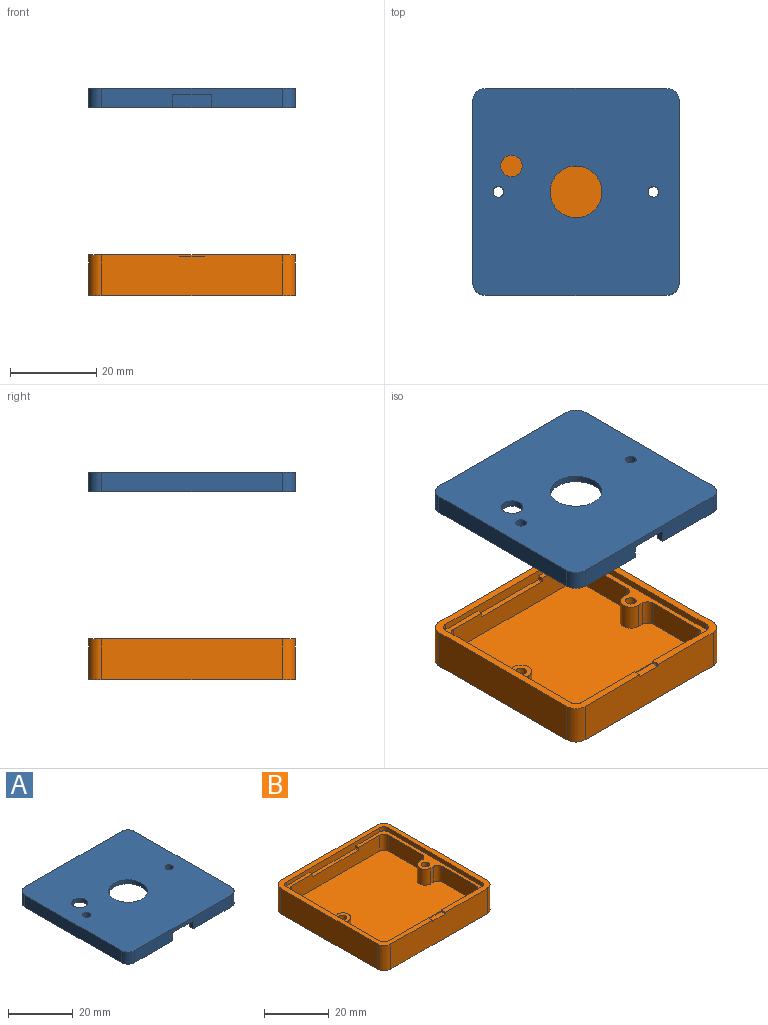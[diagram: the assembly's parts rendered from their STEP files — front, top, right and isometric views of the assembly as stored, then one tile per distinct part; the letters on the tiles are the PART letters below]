
ASSEMBLY  parts=2 mates=1
PART A: 38 faces, bbox 48x48x4.5 mm
  f0: plane 15.95x3mm, normal (0,1,0), area 47.8mm2, adj f12,f17,f33,f35
  f1: plane 42x4.5mm, normal (1,0,0), area 189mm2, adj f2,f9,f11,f12
  f2: cylinder r=3mm len=4.5mm, axis (0,0,-1), area 21.2mm2, adj f1,f3,f11,f12
  f3: plane 42x4.5mm, normal (0,1,0), area 189mm2, adj f2,f4,f11,f12
  f4: cylinder r=3mm len=4.5mm, axis (0,0,-1), area 21.2mm2, adj f3,f5,f11,f12
  f5: plane 42x4.5mm, normal (-1,0,0), area 189mm2, adj f4,f6,f11,f12
  f6: cylinder r=3mm len=4.5mm, axis (0,0,-1), area 21.2mm2, adj f5,f7,f11,f12
  f7: plane 42x4.5mm, normal (0,-1,0), area 162mm2, adj f6,f9,f11,f12,f33,f34,f35
  f8: cylinder r=1.25mm len=4.5mm, axis (0,0,-1), area 35.3mm2, adj f11,f12
  f9: cylinder r=3mm len=4.5mm, axis (0,0,-1), area 21.2mm2, adj f1,f7,f11,f12
  f10: cylinder r=1.25mm len=4.5mm, axis (0,0,-1), area 35.3mm2, adj f11,f12
  f11: plane 48x48mm, normal (0,0,1), area 2153.7mm2, adj f1,f2,f3,f4,f5,f6,f7,f8
  f12: plane 48x48mm, normal (0,0,-1), area 358mm2, adj f0,f1,f2,f3,f4,f5,f6,f7
  f13: cylinder r=2.5mm len=5mm, axis (0,0,-1), area 23.6mm2, adj f12,f14,f32,f33
  f14: plane 3x2.45mm, normal (0,-1,0), area 7.4mm2, adj f12,f13,f15,f33
  f15: cylinder r=1.8mm len=3mm, axis (0,0,-1), area 8.5mm2, adj f12,f14,f16,f33
  f16: plane 16.15x3mm, normal (1,0,0), area 48.4mm2, adj f12,f15,f17,f33
  f17: cylinder r=1.8mm len=3mm, axis (0,0,-1), area 8.5mm2, adj f0,f12,f16,f33
  f18: plane 15.95x3mm, normal (0,1,0), area 47.8mm2, adj f12,f19,f33,f34
  f19: cylinder r=1.8mm len=3mm, axis (0,0,-1), area 8.5mm2, adj f12,f18,f20,f33
  f20: plane 16.15x3mm, normal (-1,0,0), area 48.4mm2, adj f12,f19,f21,f33
  f21: cylinder r=1.8mm len=3mm, axis (0,0,-1), area 8.5mm2, adj f12,f20,f22,f33
  f22: plane 3x2.45mm, normal (0,-1,0), area 7.4mm2, adj f12,f21,f23,f33
  f23: cylinder r=2.5mm len=5mm, axis (0,0,-1), area 23.6mm2, adj f12,f22,f24,f33
  f24: plane 3x2.55mm, normal (0,1,0), area 7.7mm2, adj f12,f23,f25,f33
  f25: cylinder r=1.7mm len=3mm, axis (0,0,-1), area 8mm2, adj f12,f24,f26,f33
  f26: plane 16.25x3mm, normal (-1,0,0), area 48.8mm2, adj f12,f25,f27,f33
  f27: cylinder r=1.8mm len=3mm, axis (0,0,-1), area 8.5mm2, adj f12,f26,f28,f33
  f28: plane 40.9x3mm, normal (0,-1,0), area 122.7mm2, adj f12,f27,f29,f33
  f29: cylinder r=1.8mm len=3mm, axis (0,0,-1), area 8.5mm2, adj f12,f28,f30,f33
  f30: plane 16.25x3mm, normal (1,0,0), area 48.8mm2, adj f12,f29,f31,f33
  f31: cylinder r=1.7mm len=3mm, axis (0,0,-1), area 8mm2, adj f12,f30,f32,f33
  f32: plane 3x2.55mm, normal (0,1,0), area 7.7mm2, adj f12,f13,f31,f33
  f33: plane 46.25x44.5mm, normal (0,0,-1), area 1795.7mm2, adj f0,f7,f13,f14,f15,f16,f17,f18
  f34: plane 3x1.75mm, normal (-1,0,0), area 5.3mm2, adj f7,f12,f18,f33
  f35: plane 3x1.75mm, normal (1,0,0), area 5.3mm2, adj f0,f7,f12,f33
  f36: cylinder r=6mm len=12mm, axis (0,0,1), area 56.5mm2, adj f11,f33
  f37: cylinder r=2.5mm len=5mm, axis (0,0,-1), area 23.6mm2, adj f11,f33
PART B: 53 faces, bbox 48x48x9.5 mm
  f0: plane 26.55x12.25mm, normal (0,0,1), area 45.4mm2, adj f2,f9,f10,f12,f29,f30,f31,f50
  f1: plane 44.5x44.5mm, normal (0,0,1), area 144.7mm2, adj f2,f7,f8,f13,f14,f15,f16,f17
  f2: plane 38.4x6mm, normal (0,-1,0), area 210.4mm2, adj f0,f1,f5,f12,f13,f47,f48,f49
  f3: plane 42x9.5mm, normal (0,-1,0), area 396mm2, adj f4,f6,f40,f41,f42,f43,f44,f45
  f4: plane 48x48mm, normal (0,0,1), area 308.3mm2, adj f3,f27,f28,f29,f30,f31,f32,f33
  f5: plane 43.25x42mm, normal (0,0,1), area 1731.9mm2, adj f2,f7,f8,f9,f10,f11,f12,f13
  f6: plane 48x48mm, normal (0,0,-1), area 2286.5mm2, adj f3,f25,f26,f35,f36,f37,f38,f39
  f7: plane 14.9x6mm, normal (-1,0,0), area 89.4mm2, adj f1,f5,f15,f16
  f8: plane 14.9x6mm, normal (-1,0,0), area 89.4mm2, adj f1,f5,f13,f14
  f9: plane 21.79x6mm, normal (1,0,0), area 103.2mm2, adj f0,f5,f10,f11,f12,f52
  f10: cylinder r=1.8mm len=6mm, axis (0,0,-1), area 15.8mm2, adj f0,f5,f9,f18,f30,f52
  f11: cylinder r=1.8mm len=4mm, axis (0,0,-1), area 11.3mm2, adj f5,f9,f20,f52
  f12: cylinder r=1.8mm len=6mm, axis (0,0,-1), area 17mm2, adj f0,f2,f5,f9
  f13: cylinder r=1.8mm len=6mm, axis (0,0,-1), area 17mm2, adj f1,f2,f5,f8
  f14: cylinder r=1.8mm len=6mm, axis (0,0,-1), area 17mm2, adj f1,f5,f8,f21
  f15: cylinder r=1.8mm len=6mm, axis (0,0,-1), area 17mm2, adj f1,f5,f7,f23
  f16: cylinder r=1.8mm len=6mm, axis (0,0,-1), area 17mm2, adj f1,f5,f7,f24
  f17: cylinder r=1.8mm len=6mm, axis (0,0,-1), area 17mm2, adj f1,f5,f24,f30
  f18: plane 4x2.45mm, normal (0,-1,0), area 9.8mm2, adj f5,f10,f19,f52
  f19: cylinder r=2.5mm len=5mm, axis (0,0,-1), area 31.4mm2, adj f5,f18,f20,f52
  f20: plane 4x1.2mm, normal (0,1,0), area 4.8mm2, adj f5,f11,f19,f52
  f21: plane 6x1.2mm, normal (0,1,0), area 7.2mm2, adj f1,f5,f14,f22
  f22: cylinder r=2.5mm len=6mm, axis (0,0,-1), area 47.1mm2, adj f1,f5,f21,f23
  f23: plane 6x1.2mm, normal (0,-1,0), area 7.2mm2, adj f1,f5,f15,f22
  f24: plane 39.65x6mm, normal (0,1,0), area 237.9mm2, adj f1,f5,f16,f17
  f25: cylinder r=1.25mm len=8mm, axis (0,0,-1), area 62.8mm2, adj f1,f6
  f26: cylinder r=1.25mm len=6mm, axis (0,0,-1), area 47.1mm2, adj f6,f52
  f27: plane 40.9x1.5mm, normal (0,1,0), area 58.4mm2, adj f1,f4,f33,f34,f42,f43,f44,f45
  f28: plane 40.9x1.5mm, normal (-1,0,0), area 61.3mm2, adj f1,f4,f32,f33
  f29: plane 40.9x2.5mm, normal (0,-1,0), area 81.3mm2, adj f0,f1,f4,f31,f32,f47,f48,f49
  f30: plane 40.9x7.5mm, normal (1,0,0), area 150.7mm2, adj f0,f1,f4,f5,f10,f17,f31,f34
  f31: cylinder r=1.8mm len=1.8mm, axis (0,0,-1), area 4.2mm2, adj f0,f4,f29,f30
  f32: cylinder r=1.8mm len=1.8mm, axis (0,0,-1), area 4.2mm2, adj f1,f4,f28,f29
  f33: cylinder r=1.8mm len=1.8mm, axis (0,0,-1), area 4.2mm2, adj f1,f4,f27,f28
  f34: cylinder r=1.8mm len=1.8mm, axis (0,0,-1), area 4.2mm2, adj f1,f4,f27,f30
  f35: plane 42x9.5mm, normal (1,0,0), area 399mm2, adj f4,f6,f36,f41
  f36: cylinder r=3mm len=9.5mm, axis (0,0,-1), area 44.8mm2, adj f4,f6,f35,f37
  f37: plane 42x9.5mm, normal (0,1,0), area 399mm2, adj f4,f6,f36,f38
  f38: cylinder r=3mm len=9.5mm, axis (0,0,-1), area 44.8mm2, adj f4,f6,f37,f39
  f39: plane 42x9.5mm, normal (-1,0,0), area 399mm2, adj f4,f6,f38,f40
  f40: cylinder r=3mm len=9.5mm, axis (0,0,-1), area 44.8mm2, adj f3,f4,f6,f39
  f41: cylinder r=3mm len=9.5mm, axis (0,0,-1), area 44.8mm2, adj f3,f4,f6,f35
  f42: plane 5.6x1.75mm, normal (0,0,1), area 9.8mm2, adj f3,f27,f43,f44
  f43: cylinder r=0.2mm len=1.75mm, axis (0,-1,0), area 0.5mm2, adj f3,f27,f42,f45
  f44: cylinder r=0.2mm len=1.75mm, axis (0,-1,0), area 0.5mm2, adj f3,f27,f42,f46
  f45: plane 1.75x0.3mm, normal (-1,0,0), area 0.5mm2, adj f3,f4,f27,f43
  f46: plane 1.75x0.3mm, normal (1,0,0), area 0.5mm2, adj f3,f4,f27,f44
  f47: plane 19.6x1.25mm, normal (0,0,1), area 24.5mm2, adj f2,f29,f48,f51
  f48: cylinder r=0.2mm len=1.25mm, axis (0,-1,0), area 0.4mm2, adj f2,f29,f47,f49
  f49: plane 1.25x0.8mm, normal (-1,0,0), area 1mm2, adj f1,f2,f29,f48
  f50: plane 1.25x0.8mm, normal (1,0,0), area 1mm2, adj f0,f2,f29,f51
  f51: cylinder r=0.2mm len=1.25mm, axis (0,-1,0), area 0.4mm2, adj f2,f29,f47,f50
  f52: plane 6.89x5.5mm, normal (0,0,1), area 20.6mm2, adj f9,f10,f11,f18,f19,f20,f26
PLACE A t=(18,0,43.67)mm
PLACE B t=(18,0,0)mm
MATE cylindrical A.f10 <-> B.f25  axis (0,0,1) through (36,0,48.17)mm
